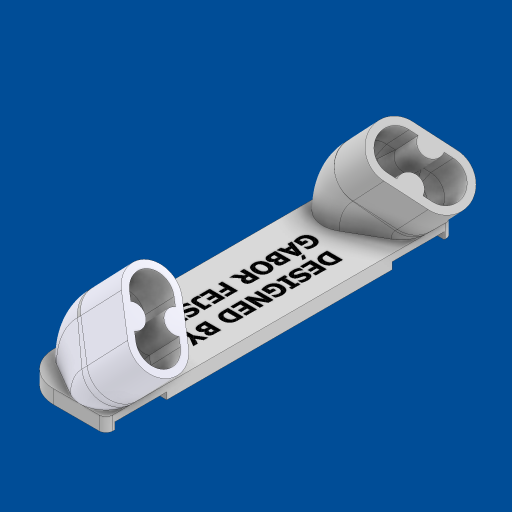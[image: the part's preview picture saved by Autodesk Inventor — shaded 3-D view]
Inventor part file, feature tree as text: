
AUTODESK INVENTOR PART (.ipt)
format: ipt  version: 2023 (Build 270158000, 158)  size: 1,113,088 bytes
history: native  units: mm
features: extrude x17, sketch x12, plane x2, revolve x2, chamfer x2, fillet x2, sweep x1, mirror x1
ambient origin geometry x8: Origin, YZ Plane, XZ Plane, XY Plane, X Axis, Y Axis, Z Axis, Center Point
bodies: Solid1 (feature_tree)
feature tree (39):
  sketch  "Sketch1"  dims[d0=100.0mm d1=25.0mm d2=7.5mm d3=7.5mm d4=60.0deg d5=15.0mm d6=11.0mm d7=11.0mm d8=15.0mm d11=135.0deg]
  plane  "Work Plane1"
  sweep  "Sweep1"
  extrude  "Extrusion1"  Depth=4.0mm TaperAngle=0.0deg
  revolve  "Revolution1"  Angle=45.0deg
  sketch  "Sketch6"  dims[d31=10.0mm d32=45.0deg]
  extrude  "Extrusion4"  TaperAngle=45.0deg  [1 undecoded]
  extrude  "Extrusion5"  Depth=10.0mm
  sketch  "Sketch7"  dims[d33=10.0mm d34=10.0mm]
  extrude  "Extrusion6"  Depth=10.0mm
  extrude  "Extrusion7"  Depth=15.0mm
  mirror  "Mirror4"
  plane  "Work Plane9"
  extrude  "Extrusion8"  Depth=5.5mm
  revolve  "Revolution2"  [1 undecoded]
  extrude  "Extrusion9"  Depth=6.5mm
  sketch  "Sketch19"  dims[d60=5.5mm d61=5.5mm]
  extrude  "Extrusion10"  Depth=15.0mm TaperAngle=0.0deg
  extrude  "Extrusion11"  Depth=10.0mm
  extrude  "Extrusion12"  TaperAngle=90.0deg  [1 undecoded]
  sketch  "Sketch21"  dims[d65=2.0mm d66=6.5mm]
  extrude  "Extrusion13"  Depth=10.0mm
  chamfer  "Chamfer3"  Distance=5.5mm
  extrude  "Extrusion15"  Depth=10.0mm
  extrude  "Extrusion18"  Depth=10.0mm
  fillet  "Fillet2"  Radius=11.0mm
  fillet  "Fillet3"  Radius=11.0mm
  extrude  "Extrusion19"  Depth=10.0mm
  extrude  "Extrusion20"  Depth=10.0mm
  extrude  "Extrusion21"  Depth=10.0mm
  extrude  "Extrusion22"  Depth=10.0mm TaperAngle=0.0deg
  chamfer  "Chamfer6"  Distance=10.0mm
  sketch  "Sketch3"  dims[d12=0.0mm d13=0.0mm d14=4.0mm d15=0.0mm]
  sketch  "Sketch5"  dims[d29=11.389087mm d30=45.0deg]
  sketch  "Sketch14"  dims[d35=45.0deg d37=10.0mm]
  sketch  "Sketch15"  dims[d38=0.977384mm d57=15.0mm]
  sketch  "Sketch20"  dims[d63=11.0mm d64=11.0mm]
  sketch  "Sketch22"  dims[d67=6.5mm d68=15.0mm d69=0.0mm]
  sketch  "Sketch23"  dims[d70=325.0mm d71=0.0mm d72=7.5mm d73=90.0deg d74=7.5mm d75=5.5mm d76=5.5mm d77=15.0mm d78=11.0mm d79=11.0mm d80=2.0mm d81=6.5mm d82=6.5mm d83=10.0mm d84=0.0mm d93=10.0mm d94=0.0mm d115=20.0mm d116=0.0mm d131=8.726646mm d132=300.0mm d133=0.0mm d134=15.0mm d135=300.0mm d136=0.0mm d137=11.0mm d138=11.0mm d139=2.0mm d140=6.5mm d141=6.5mm d142=10.0mm d143=0.0mm d144=40.0mm d145=0.0mm d146=25.0mm d147=100.0mm d150=15.0mm d151=5.5mm d152=2.0mm d153=0.0mm d156=2.0mm d157=4.0mm d158=45.0deg d162=549.891mm d163=50.0mm d164=100.0mm d167=2.5mm d169=15.0mm d170=17.5mm d171=17.5mm d174=10.0mm d175=300.0mm d176=0.0mm d177=7.5mm d183=2.0mm d184=0.0mm d185=2.0mm d186=10.0mm d187=3.0mm d188=0.0mm d189=15.0mm d190=0.0mm d191=1.0mm d192=0.0mm d193=6.5mm d194=5.0mm d195=0.0mm d199=2.0mm d200=4.0mm d201=45.0deg d178=0.872665mm d196=0.5mm d197=0.872665mm]
note: 3 required parameter values undecoded (feature->parameter linkage not recoverable at this tier; creation-order binding heuristic only, values carry confidence <= 0.55)